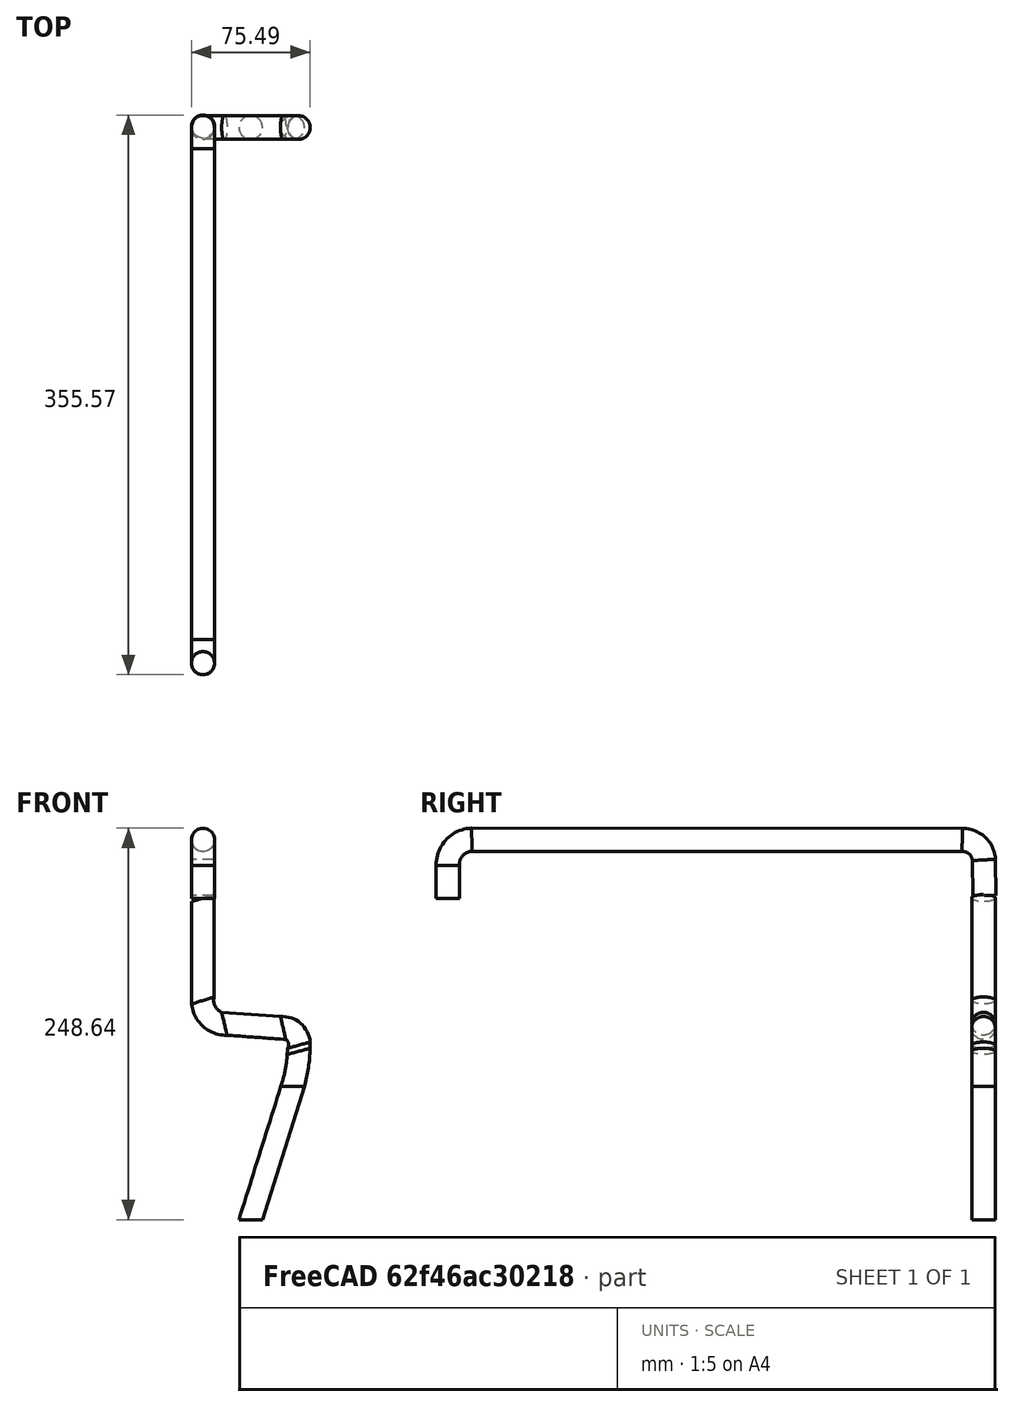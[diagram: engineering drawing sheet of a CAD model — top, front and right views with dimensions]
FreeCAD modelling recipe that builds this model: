
FCSTD DOCUMENT  (FreeCAD 0.18R16110 (Git))
Label: headstruct
License: All rights reserved
LicenseURL: http://en.wikipedia.org/wiki/All_rights_reserved
objects: Sketcher::SketchObject×4, Part::Sweep×2, Part::Mirroring×1
note: 7 computed .brp shape members not serialized (recipe doc carries the construction recipe); baked Part::Feature solids carry a one-line shape summary decoded from their .brp

FEATURE [Sketcher::SketchObject] Sketch
  Placement = pos=(0,0,0) rot=(-1,0,0;3.14159rad)
  sketch-geometry (1):
    g0: Circle CenterX=0.382568 CenterY=-0.027475 CenterZ=0 NormalX=0 NormalY=0 NormalZ=1 AngleXU=0 Radius=7.5
  constraints (1):
    c: Radius(g0) = 7.5
FEATURE [Sketcher::SketchObject] Sketch001
  MapMode = 3
  Placement = pos=(0,0,0) rot=(-1,0,0;1.5708rad)
  Support = -> [Sketch]
  sketch-geometry (9):
    g0: LineSegment StartX=30.4444 StartY=-106.823 StartZ=0 EndX=30.5977 EndY=-110.754 EndZ=0
    g1: ArcOfCircle CenterX=-54.7737 CenterY=-110.146 CenterZ=0 NormalX=0 NormalY=0 NormalZ=1 AngleXU=0 Radius=85.2828 StartAngle=0.0389758 EndAngle=0.30456
    g2: LineSegment StartX=21.093 StartY=-121.378 StartZ=0 EndX=-16.253 EndY=-124.075 EndZ=0
    g3: LineSegment StartX=-30.2679 StartY=-139.139 StartZ=0 EndX=-30.2679 EndY=-204.139 EndZ=0
    g4: ArcOfCircle CenterX=-15.1649 CenterY=-139.139 CenterZ=0 NormalX=0 NormalY=0 NormalZ=1 AngleXU=0 Radius=15.1029 StartAngle=1.6429 EndAngle=3.14159
    g5: ArcOfCircle CenterX=20.3544 CenterY=-111.153 CenterZ=0 NormalX=0 NormalY=0 NormalZ=1 AngleXU=0 Radius=10.251 StartAngle=4.78449 EndAngle=6.32216
    g6: LineSegment StartX=0.012 StartY=-0.012 StartZ=0 EndX=18.8737 EndY=-41.6474 EndZ=0
    g7: LineSegment StartX=26.5964 StartY=-84.5842 StartZ=0 EndX=24.0276 EndY=-60.5671 EndZ=0
    g8: ArcOfCircle CenterX=-37.3897 CenterY=-67.136 CenterZ=0 NormalX=0 NormalY=0 NormalZ=1 AngleXU=0 Radius=61.7677 StartAngle=0.10655 EndAngle=0.425364
  constraints (9):
    c: Tangent(g0,g1) = 1.5708
    c: Vertical(g3)
    c: Tangent(g3,g4) = -1.5708
    c: Tangent(g2,g4) = -1.5708
    c: Tangent(g2,g5) = 1.5708
    c: Tangent(g0,g5) = 1.5708
    c: Distance(g3) = 65
    c: Tangent(g7,g8) = -1.5708
    c: Tangent(g6,g8) = 1.5708
FEATURE [Part::Sweep] Sweep
  Frenet = false
  Sections = -> [Sketch]
  Solid = false
  Spine = -> Sketch001
  Transition = 1
FEATURE [Part::Mirroring] Part__Mirroring  label="Sweep (Mirror #1)"
  Base = (0,170,0)
  Normal = (0,1,0)
  Source = -> Sweep
FEATURE [Sketcher::SketchObject] Sketch002
  Placement = pos=(-30,0,0) rot=(0.57735,0.57735,0.57735;2.0944rad)
  sketch-geometry (6):
    g0: LineSegment StartX=-0.189023 StartY=204.492 StartZ=0 EndX=-0.189023 EndY=225.553 EndZ=0
    g1: LineSegment StartX=15.4943 StartY=241.228 StartZ=0 EndX=326.944 EndY=241.066 EndZ=0
    g2: LineSegment StartX=340.193 StartY=228.021 StartZ=0 EndX=340.556 EndY=205.454 EndZ=0
    g3: ArcOfCircle CenterX=15.4862 CenterY=225.553 CenterZ=0 NormalX=0 NormalY=0 NormalZ=1 AngleXU=0 Radius=15.6752 StartAngle=1.57028 EndAngle=3.14159
    g4: ArcOfCircle CenterX=326.938 CenterY=227.808 CenterZ=0 NormalX=0 NormalY=0 NormalZ=1 AngleXU=0 Radius=13.2576 StartAngle=0.0160581 EndAngle=1.57028
    g5: GeomPoint X=-0.189023 Y=204.492 Z=0
  constraints (6):
    c: Tangent(g0,g3) = 1.5708
    c: Tangent(g1,g3) = 1.5708
    c: Tangent(g2,g4) = 1.5708
    c: Tangent(g1,g4) = 1.5708
    c: Coincident(g0,g5)
    c: Vertical(g0)
FEATURE [Sketcher::SketchObject] Sketch003
  Placement = pos=(0,0,204) rot=(0,0,1;0rad)
  sketch-geometry (1):
    g0: Circle CenterX=-29.9487 CenterY=-0.265575 CenterZ=0 NormalX=0 NormalY=0 NormalZ=1 AngleXU=0 Radius=7.33764
FEATURE [Part::Sweep] Sweep001
  Frenet = false
  Sections = -> [Sketch003]
  Solid = false
  Spine = -> Sketch002
  Transition = 1
